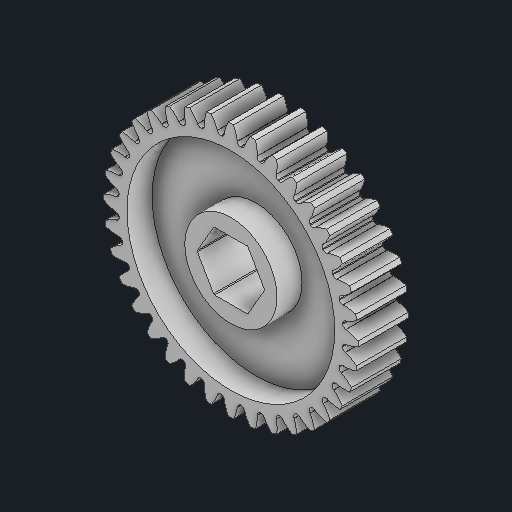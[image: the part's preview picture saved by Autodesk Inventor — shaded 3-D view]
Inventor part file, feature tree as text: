
AUTODESK INVENTOR PART (.ipt)
format: ipt  version: 2024.2 (Build 282272000, 272)  size: 1,499,136 bytes
history: native  units: in
note: dims shown in document units (in); Inventor stores cm internally (conversion verified against a paired STEP export)
features: extrude x3, sketch x3, other x3
ambient origin geometry x8: Origin, YZ Plane, XZ Plane, XY Plane, X Axis, Y Axis, Z Axis, Center Point
bodies: Solid1 (feature_tree), Solid2 (feature_tree), Solid3 (feature_tree)
feature tree (9):
  extrude  "Extrusion1"  Depth=1.0in TaperAngle=0.0deg
  extrude  "Extrusion2"  Depth=1.0in TaperAngle=0.0deg
  extrude  "Extrusion3"  Depth=1.0in TaperAngle=0.0deg
  sketch  "Sketch1"  dims[d0=1.0in d1=1.0in d2=0.0in]
  sketch  "Sketch2"  dims[d3=0.25in d4=1.0in d5=0.0in]
  sketch  "Sketch3"  dims[d6=0.25in d7=1.0in d8=0.0in]
  other  "2303-4008-0036_Gear Blank_1:1"
  other  "2806-0005-0004_91390A117_2:1"
  other  "2806-0005-0004_91390A117_3:1"
